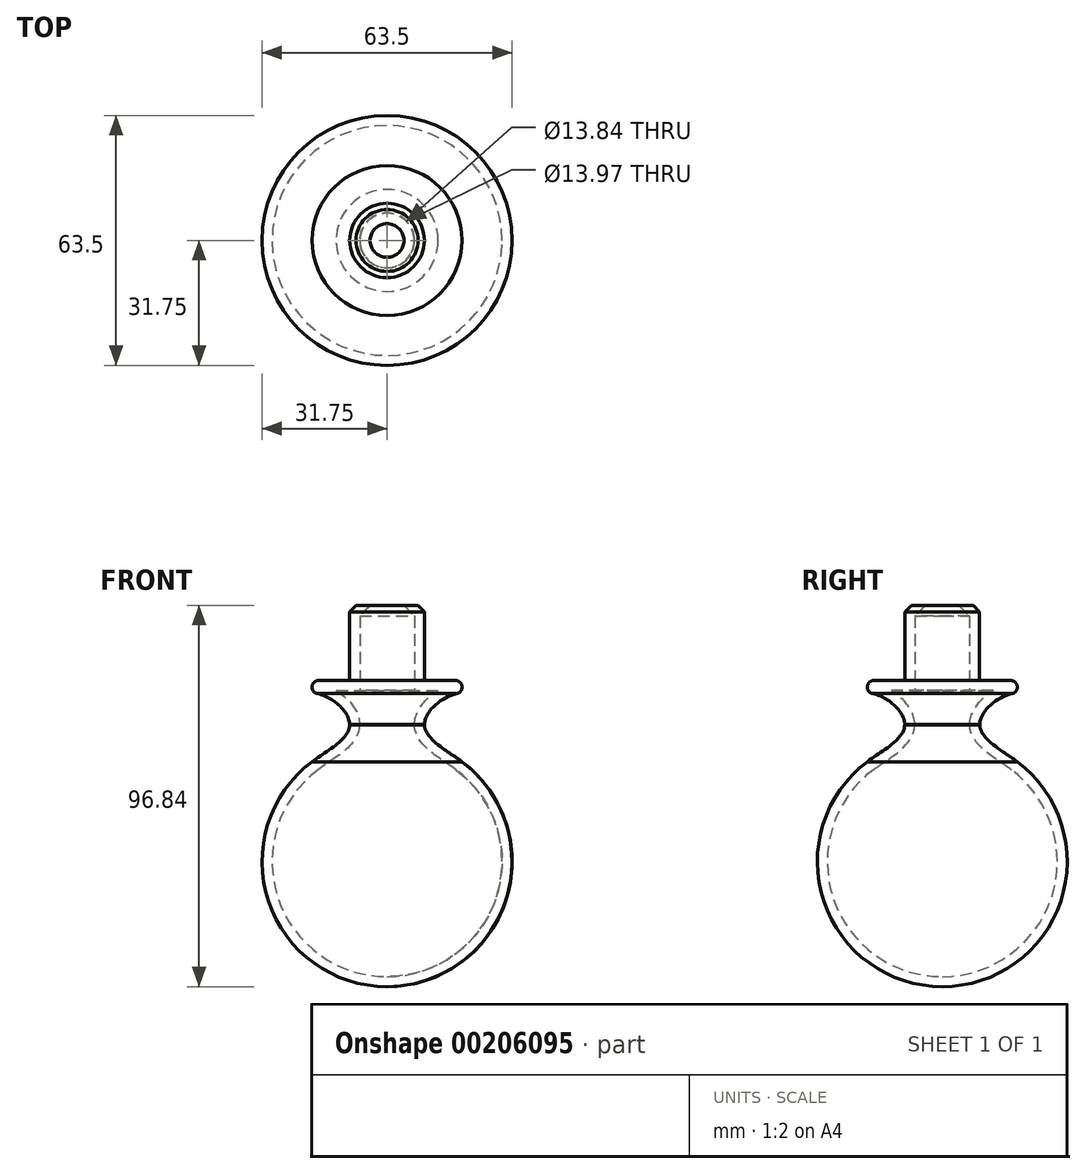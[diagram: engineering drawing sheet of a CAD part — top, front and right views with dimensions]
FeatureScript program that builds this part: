
annotation { "Feature Type Name" : "Feature", "Feature Type Description" : "" }
export const myFeature = defineFeature(function(context is Context, id is Id, definition is map)
    precondition{}
    {
        {
            var Q0;
            Q0=qCreatedBy(makeId("Front.planeOp"),FACE);
            var sketch = newSketch(context, id + "F0", { "sketchPlane" : qUnion([Q0])});
            skArc(sketch, "E0", {"start": v(0, 31.75) * mm, "mid": v(-31.75, 0) * mm, "end": v(0, -31.75) * mm});
            skLineSegment(sketch, "E1", {"start": v(0, -31.75) * mm, "end": v(0, 31.75) * mm});
            skSolve(sketch);
        }
        {
            var Q0;
            Q0=makeQuery(id+"F0.imprint","IMPRINT",FACE,{"disambiguationData":[TD([[makeQuery(id+"F0.imprint","IMPRINT",EDGE,{"derivedFrom":sQuery(id+"F0.wireOp",EDGE,"E0")}),1.0]])]});
            var Q1;
            Q1=sQuery(id+"F0.wireOp",EDGE,"E1");
            revolve(context, id + "F1", {"entities" : qUnion([Q0]), "axis" : qUnion([Q1]), "revolveType" : RevolveType.FULL});
        }
        {
            var Q0;
            Q0=qCreatedBy(makeId("Top.planeOp"),FACE);
            cPlane(context, id + "F2", {"entities" : qUnion([Q0]), "cplaneType" : CPlaneType.OFFSET, "offset" : 44.45 * mm, "width" : 152.4 * mm, "height" : 152.4 * mm});
        }
        {
            var Q0;
            Q0=qCreatedBy(id+"F2.planeOp",FACE);
            var sketch = newSketch(context, id + "F3", { "sketchPlane" : qUnion([Q0])});
            skCircle(sketch, "E2", {"center": v(0, 0) * mm, "radius": 9.53 * mm});
            skSolve(sketch);
        }
        {
            var Q0;
            Q0=makeQuery(id+"F3.imprint","IMPRINT",FACE,{"disambiguationData":[TD([[makeQuery(id+"F3.imprint","IMPRINT",EDGE,{"derivedFrom":sQuery(id+"F3.wireOp",EDGE,"E2")}),1.0]])]});
            extrude(context, id + "F4", {"entities" : qUnion([Q0]), "operationType" : NewBodyOperationType.ADD, "endBound" : BoundingType.UP_TO_NEXT, "oppositeDirection" : true, "depth" : 34.3 * mm});
        }
        {
            var Q0;
            Q0=makeQuery(id+"F4.opExtrude","CAP_FACE",FACE,{"disambiguationData":[OSD([sQuery(id+"F3.wireOp",EDGE,"E2")])],"isStart":true});
            var sketch = newSketch(context, id + "F5", { "sketchPlane" : qUnion([Q0])});
            skCircle(sketch, "E3", {"center": v(0, 0) * mm, "radius": 19.05 * mm});
            skSolve(sketch);
        }
        {
            var Q0;
            Q0=makeQuery(id+"F5.imprint","IMPRINT",FACE,{"disambiguationData":[TD([[makeQuery(id+"F5.imprint","IMPRINT",EDGE,{"derivedFrom":sQuery(id+"F5.wireOp",EDGE,"E3")}),1.0]])]});
            var Q1;
            Q1=makeQuery(id+"F5.imprint","IMPRINT",FACE,{"disambiguationData":[TD([[makeQuery(id+"F5.imprint","IMPRINT",EDGE,{"derivedFrom":makeQuery(id+"F4.opExtrude","CAP_EDGE",EDGE,{"disambiguationData":[OSD([sQuery(id+"F3.wireOp",EDGE,"E2")])],"isStart":true})}),1.0]])]});
            extrude(context, id + "F6", {"entities" : qUnion([Q0, Q1]), "operationType" : NewBodyOperationType.ADD, "endBound" : BoundingType.SYMMETRIC, "depth" : 3.17 * mm});
        }
        {
            var Q0;
            Q0=makeQuery(id+"F6.opExtrude","CAP_FACE",FACE,{"disambiguationData":[OSD([sQuery(id+"F5.wireOp",EDGE,"E3")])],"isStart":false});
            var sketch = newSketch(context, id + "F7", { "sketchPlane" : qUnion([Q0])});
            skCircle(sketch, "E4", {"center": v(0, 0) * mm, "radius": 9.46 * mm});
            skSolve(sketch);
        }
        {
            var Q0;
            Q0=makeQuery(id+"F7.imprint","IMPRINT",FACE,{"disambiguationData":[TD([[makeQuery(id+"F7.imprint","IMPRINT",EDGE,{"derivedFrom":sQuery(id+"F7.wireOp",EDGE,"E4")}),1.0]])]});
            extrude(context, id + "F8", {"entities" : qUnion([Q0]), "operationType" : NewBodyOperationType.ADD, "depth" : 19.05 * mm});
        }
        {
            var Q0;
            Q0=makeQuery(id+"F8.opExtrude","CAP_EDGE",EDGE,{"disambiguationData":[OSD([sQuery(id+"F7.wireOp",EDGE,"E4")])],"isStart":false});
            chamfer(context, id + "F9", {"entities" : qUnion([Q0]), "width" : 1.59 * mm, "tangentPropagation" : true});
        }
        {
            var Q0;
            Q0=qCreatedBy(makeId("Right.planeOp"),FACE);
            var sketch = newSketch(context, id + "F10", { "sketchPlane" : qUnion([Q0])});
            skLineSegment(sketch, "E5", {"start": v(0, 25.4) * mm, "end": v(0, 42.86) * mm});
            skLineSegment(sketch, "E6", {"start": v(0, 42.86) * mm, "end": v(-19.05, 42.86) * mm});
            skFitSpline(sketch, "E7", {"points": [v(-19.05, 42.86) * mm, v(-9.53, 34.74) * mm, v(-19.05, 25.4) * mm], "startDerivative": vector(27.69, -0.92) * mm, "endDerivative": vector(-22.64, -16.9) * mm});
            skLineSegment(sketch, "E8", {"start": v(0, 25.4) * mm, "end": v(-19.05, 25.4) * mm});
            skLineSegment(sketch, "E9", {"start": v(-19.05, 42.86) * mm, "end": v(-19.05, 25.4) * mm, "construction": true});
            skCircle(sketch, "E10", {"center": v(0, 0) * mm, "radius": 31.75 * mm, "construction": true});
            skSolve(sketch);
        }
        {
            var Q0;
            Q0=makeQuery(id+"F10.imprint","IMPRINT",FACE,{"disambiguationData":[TD([[makeQuery(id+"F10.imprint","IMPRINT",EDGE,{"derivedFrom":sQuery(id+"F10.wireOp",EDGE,"E5")}),1.0]])]});
            var Q1;
            Q1=sQuery(id+"F10.wireOp",EDGE,"E5");
            revolve(context, id + "F11", {"operationType" : NewBodyOperationType.ADD, "entities" : qUnion([Q0]), "axis" : qUnion([Q1]), "revolveType" : RevolveType.FULL});
        }
        {
            var Q0;
            Q0=makeQuery(id+"F11.boolean.opBoolean","MERGE",EDGE,{"derivedFrom":[makeQuery(id+"F6.opExtrude","CAP_EDGE",EDGE,{"disambiguationData":[OSD([sQuery(id+"F5.wireOp",EDGE,"E3")])],"isStart":true}),makeQuery(id+"F11.opRevolve","SWEPT_EDGE",EDGE,{"disambiguationData":[OSD([sQuery(id+"F10.wireOp",EDGE,"E6"),sQuery(id+"F10.wireOp",EDGE,"E7")])]})]});
            var Q1;
            Q1=makeQuery(id+"F6.opExtrude","CAP_EDGE",EDGE,{"disambiguationData":[OSD([sQuery(id+"F5.wireOp",EDGE,"E3")])],"isStart":false});
            var Q2;
            Q2=makeQuery(id+"F8.opExtrude","CAP_EDGE",EDGE,{"disambiguationData":[OSD([sQuery(id+"F7.wireOp",EDGE,"E4")])],"isStart":true});
            fillet(context, id + "F12", {"entities" : qUnion([Q0, Q1, Q2]), "radius" : 1.65 * mm, "tangentPropagation" : true, "allowEdgeOverflow" : false});
        }
        {
            var Q0;
            Q0=makeQuery(id+"F8.opExtrude","CAP_FACE",FACE,{"disambiguationData":[OSD([sQuery(id+"F7.wireOp",EDGE,"E4")])],"isStart":false});
            shell(context, id + "F13", {"entities" : qUnion([Q0]), "thickness" : 2.54 * mm});
        }
    });
